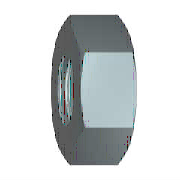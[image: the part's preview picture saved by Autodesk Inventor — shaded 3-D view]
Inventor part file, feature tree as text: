
AUTODESK INVENTOR PART (.ipt)
format: ipt  version: 2023.2 (Build 272271030, 271C)  size: 162,304 bytes
history: native  units: mm (DEFAULTED — no unit token found)
features: sketch x3, chamfer x1, hole x1, other x1, plane x1
ambient origin geometry x7: Origin, YZ Plane, XZ Plane, X Axis, Y Axis, Z Axis, Center Point
bodies: Solid1 (feature_tree), Body (feature_tree)
feature tree (7):
  chamfer  "Chamfer1"  Angle=30.0deg  [1 undecoded]
  hole  "Thread"  [1 undecoded]
  other  "Work Axis1"
  plane  "Work Plane1"
  sketch  "Sketch1"  dims[d0=18.475209mm]
  sketch  "Sketch2"  dims[d1=8.4mm]
  sketch  "Sketch3"  dims[d2=0.0mm d3=30.0deg d4=30.0deg d5=14.6mm d6=14.6mm d7=90.0deg d25=8.376mm d26=6.0mm d27=4.0mm d28=2.0mm d29=14.3117mm d30=8.0mm d31=20.594885mm d8=0.811899mm d9=30.0deg d10=0.811899mm d11=30.0deg d13=0.0mm d14=0.0mm d39=0.0mm d40=0.811899mm d41=0.811899mm d42=0.0mm]
note: 2 required parameter values undecoded (feature->parameter linkage not recoverable at this tier; creation-order binding heuristic only, values carry confidence <= 0.55)
